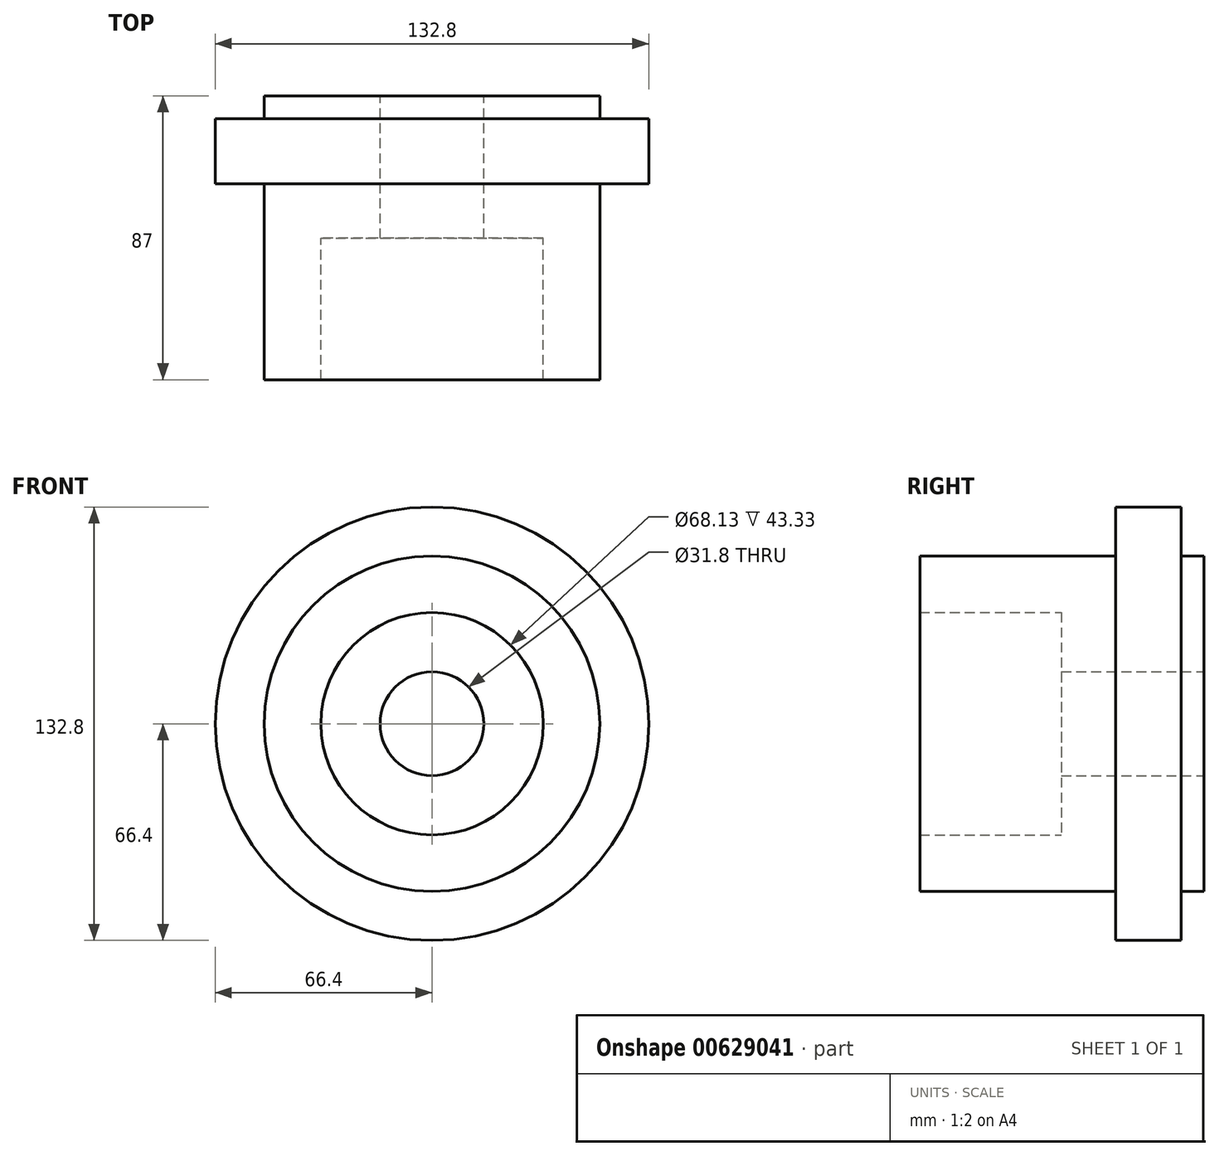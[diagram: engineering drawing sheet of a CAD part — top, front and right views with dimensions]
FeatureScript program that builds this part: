
annotation { "Feature Type Name" : "Feature", "Feature Type Description" : "" }
export const myFeature = defineFeature(function(context is Context, id is Id, definition is map)
    precondition{}
    {
        {
            var Q0;
            Q0=qCreatedBy(makeId("Right.planeOp"),FACE);
            var sketch = newSketch(context, id + "F0", { "sketchPlane" : qUnion([Q0])});
            skLineSegment(sketch, "E0", {"start": v(0, 0) * mm, "end": v(-199.8, 0) * mm, "construction": true});
            skLineSegment(sketch, "E1", {"start": v(0, 0) * mm, "end": v(160.58, 0) * mm, "construction": true});
            skLineSegment(sketch, "E2", {"start": v(-6.86, 66.4) * mm, "end": v(-6.86, 51.4) * mm});
            skLineSegment(sketch, "E3", {"start": v(-6.86, 51.4) * mm, "end": v(0.14, 51.4) * mm});
            skLineSegment(sketch, "E4", {"start": v(0.14, 51.4) * mm, "end": v(0.14, 15.9) * mm});
            skLineSegment(sketch, "E5", {"start": v(-86.86, 34.07) * mm, "end": v(-43.53, 34.07) * mm});
            skLineSegment(sketch, "E6", {"start": v(0.14, 15.9) * mm, "end": v(-83.6, 15.9) * mm, "construction": true});
            skLineSegment(sketch, "E7", {"start": v(-43.53, 34.07) * mm, "end": v(-43.53, 15.9) * mm});
            skLineSegment(sketch, "E8", {"start": v(-43.53, 15.9) * mm, "end": v(0.14, 15.9) * mm});
            skLineSegment(sketch, "E9", {"start": v(-26.86, 66.4) * mm, "end": v(-26.86, 51.4) * mm});
            skLineSegment(sketch, "E10", {"start": v(-26.86, 51.4) * mm, "end": v(-86.86, 51.4) * mm});
            skLineSegment(sketch, "E11", {"start": v(-26.86, 66.4) * mm, "end": v(-6.86, 66.4) * mm});
            skLineSegment(sketch, "E12", {"start": v(-86.86, 51.4) * mm, "end": v(-86.86, 34.07) * mm});
            skLineSegment(sketch, "E13", {"start": v(-6.86, 66.4) * mm, "end": v(-6.86, 0) * mm, "construction": true});
            skLineSegment(sketch, "E14", {"start": v(-43.53, 34.07) * mm, "end": v(-154.08, 34.07) * mm, "construction": true});
            skLineSegment(sketch, "E15", {"start": v(-154.08, 34.07) * mm, "end": v(-154.08, 0) * mm, "construction": true});
            skLineSegment(sketch, "E16", {"start": v(-83.6, 15.9) * mm, "end": v(-83.6, 0) * mm, "construction": true});
            skSolve(sketch);
        }
        {
            var Q0;
            Q0 = qSketchRegion(id + "F0", true);
            var Q1;
            Q1=sQuery(id+"F0.wireOp",EDGE,"E0");
            revolve(context, id + "F1", {"entities" : qUnion([Q0]), "axis" : qUnion([Q1]), "revolveType" : RevolveType.FULL});
        }
    });
